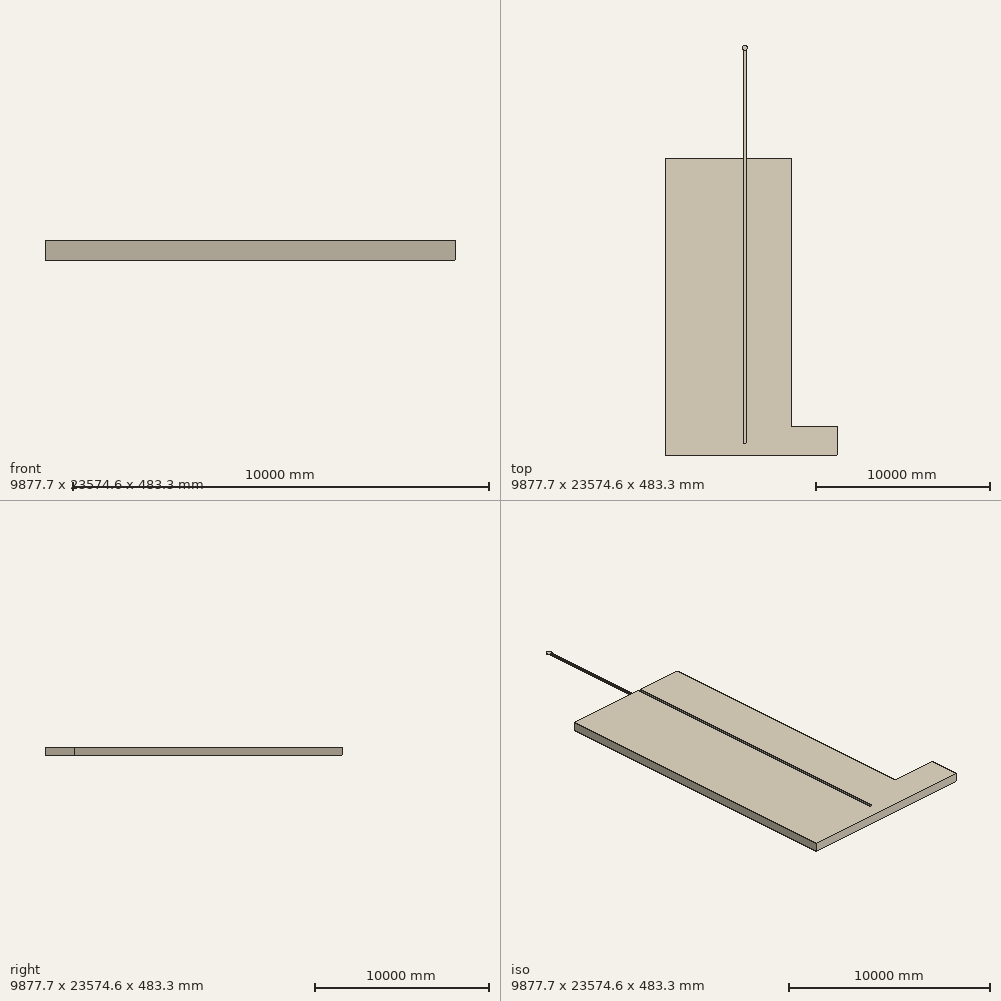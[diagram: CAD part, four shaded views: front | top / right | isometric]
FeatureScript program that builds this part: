
annotation { "Feature Type Name" : "Feature", "Feature Type Description" : "" }
export const myFeature = defineFeature(function(context is Context, id is Id, definition is map)
    precondition{}
    {
        {
            var Q0;
            Q0=qCreatedBy(makeId("Front.planeOp"),FACE);
            var sketch = newSketch(context, id + "F0", { "sketchPlane" : qUnion([Q0])});
            skLineSegment(sketch, "E0.bottom", {"start": v(-11.78, 29.24) * mm, "end": v(-162.05, 29.24) * mm});
            skLineSegment(sketch, "E0.top", {"start": v(-11.78, 3.84) * mm, "end": v(-162.05, 3.84) * mm});
            skLineSegment(sketch, "E0.left", {"start": v(-162.05, 29.24) * mm, "end": v(-162.05, 3.84) * mm});
            skLineSegment(sketch, "E0.right", {"start": v(-11.78, 29.24) * mm, "end": v(-11.78, 3.84) * mm});
            skSolve(sketch);
        }
        {
            var Q0;
            Q0=makeQuery(id+"F0.imprint","IMPRINT",FACE,{"disambiguationData":[TD([[makeQuery(id+"F0.imprint","IMPRINT",EDGE,{"derivedFrom":sQuery(id+"F0.wireOp",EDGE,"E0.bottom")}),1.0]])]});
            extrude(context, id + "F1", {"entities" : qUnion([Q0]), "depth" : 22860 * mm});
        }
        {
            var Q0;
            Q0=makeQuery(id+"F1.opExtrude","SWEPT_FACE",FACE,{"disambiguationData":[OSD([sQuery(id+"F0.wireOp",EDGE,"E0.bottom")])]});
            shell(context, id + "F2", {"entities" : qUnion([Q0]), "thickness" : 1.59 * mm});
        }
        {
            var Q0;
            Q0=makeQuery(id+"F2.opShell","OFFSET_FACE",FACE,{"disambiguationData":[OSD([sQuery(id+"F0.wireOp",EDGE,"E0.top")])]});
            var sketch = newSketch(context, id + "F3", { "sketchPlane" : qUnion([Q0])});
            skCircle(sketch, "E1", {"center": v(-71.32, -114.14) * mm, "radius": 143.58 * mm});
            skSolve(sketch);
        }
        {
            var Q0;
            {var subQ1=sQuery(id+"F0.wireOp",EDGE,"E0.top");var subQ2=makeQuery(id+"F2.opShell","OFFSET_EDGE",EDGE,{"disambiguationData":[OSD([subQ1]),TDD([makeQuery(id+"F1.opExtrude","CAP_EDGE",EDGE,{"disambiguationData":[OSD([subQ1])],"isStart":true})])]});Q0=makeQuery(id+"F3.imprint","IMPRINT",FACE,{"disambiguationData":[TD([[makeQuery(id+"F3.imprint","IMPRINT",EDGE,{"derivedFrom":subQ2}),-1.0]])]});}
            var Q1;
            {var subQ1=sQuery(id+"F0.wireOp",EDGE,"E0.top");var subQ6=makeQuery(id+"F2.opShell","OFFSET_EDGE",EDGE,{"disambiguationData":[OSD([subQ1]),TDD([makeQuery(id+"F1.opExtrude","CAP_EDGE",EDGE,{"disambiguationData":[OSD([subQ1])],"isStart":true})])]});Q1=makeQuery(id+"F3.imprint","IMPRINT",FACE,{"disambiguationData":[TD([[makeQuery(id+"F3.imprint","IMPRINT",EDGE,{"derivedFrom":subQ6}),1.0]])]});}
            var Q2;
            {var subQ0=sQuery(id+"F3.wireOp",EDGE,"E1");var subQ1=sQuery(id+"F0.wireOp",EDGE,"E0.top");var subQ2=makeQuery(id+"F2.opShell","OFFSET_EDGE",EDGE,{"disambiguationData":[OSD([subQ1,sQuery(id+"F0.wireOp",EDGE,"E0.left")])]});var subQ4=makeQuery(id+"F3.imprint","INTERSECT",VERTEX,{"derivedFrom":[subQ2,subQ0]});Q2=makeQuery(id+"F3.imprint","IMPRINT",FACE,{"disambiguationData":[TD([[makeQuery(id+"F3.imprint","IMPRINT",EDGE,{"disambiguationData":[TD([[subQ4,1.0]])],"derivedFrom":subQ0}),1.0]])]});}
            var Q3;
            {var subQ1=sQuery(id+"F0.wireOp",EDGE,"E0.top");var subQ2=makeQuery(id+"F2.opShell","OFFSET_EDGE",EDGE,{"disambiguationData":[OSD([subQ1]),TDD([makeQuery(id+"F1.opExtrude","CAP_EDGE",EDGE,{"disambiguationData":[OSD([subQ1])],"isStart":true})])]});Q3=makeQuery(id+"F3.imprint","IMPRINT",FACE,{"disambiguationData":[TD([[makeQuery(id+"F3.imprint","IMPRINT",EDGE,{"derivedFrom":subQ2}),-1.0]])]});}
            var Q4;
            {var subQ1=sQuery(id+"F0.wireOp",EDGE,"E0.top");var subQ6=makeQuery(id+"F2.opShell","OFFSET_EDGE",EDGE,{"disambiguationData":[OSD([subQ1]),TDD([makeQuery(id+"F1.opExtrude","CAP_EDGE",EDGE,{"disambiguationData":[OSD([subQ1])],"isStart":true})])]});Q4=makeQuery(id+"F3.imprint","IMPRINT",FACE,{"disambiguationData":[TD([[makeQuery(id+"F3.imprint","IMPRINT",EDGE,{"derivedFrom":subQ6}),1.0]])]});}
            extrude(context, id + "F4", {"entities" : qUnion([Q0, Q1, Q2, Q3, Q4]), "operationType" : NewBodyOperationType.ADD, "depth" : 25.4 * mm});
        }
        {
            var Q0;
            Q0=makeQuery(id+"F2.opShell","OFFSET_FACE",FACE,{"disambiguationData":[OSD([sQuery(id+"F0.wireOp",EDGE,"E0.top")])]});
            var sketch = newSketch(context, id + "F5", { "sketchPlane" : qUnion([Q0])});
            skLineSegment(sketch, "E2.bottom", {"start": v(2602.83, -6484.61) * mm, "end": v(-4650.3, -6484.61) * mm});
            skLineSegment(sketch, "E2.top", {"start": v(2602.83, -21867.56) * mm, "end": v(-4650.3, -21867.56) * mm});
            skLineSegment(sketch, "E2.left", {"start": v(2602.83, -6484.61) * mm, "end": v(2602.83, -21867.56) * mm});
            skLineSegment(sketch, "E2.right", {"start": v(-4650.3, -6484.61) * mm, "end": v(-4650.3, -21867.56) * mm});
            skLineSegment(sketch, "E3.bottom", {"start": v(-4650.3, -21867.56) * mm, "end": v(5227.4, -21867.56) * mm});
            skLineSegment(sketch, "E3.top", {"start": v(-4650.3, -23545.2) * mm, "end": v(5227.4, -23545.2) * mm});
            skLineSegment(sketch, "E3.left", {"start": v(-4650.3, -21867.56) * mm, "end": v(-4650.3, -23545.2) * mm});
            skLineSegment(sketch, "E3.right", {"start": v(5227.4, -21867.56) * mm, "end": v(5227.4, -23545.2) * mm});
            skSolve(sketch);
        }
        {
            var Q0;
            {var subQ0=sQuery(id+"F5.wireOp",EDGE,"E2.right");Q0=makeQuery(id+"F5.imprint","IMPRINT",FACE,{"disambiguationData":[TD([[makeQuery(id+"F5.imprint","IMPRINT",EDGE,{"derivedFrom":subQ0}),1.0]])]});}
            var Q1;
            Q1=makeQuery(id+"F5.imprint","IMPRINT",FACE,{"disambiguationData":[TD([[makeQuery(id+"F5.imprint","IMPRINT",EDGE,{"derivedFrom":sQuery(id+"F5.wireOp",EDGE,"E3.top")}),1.0]])]});
            var Q2;
            {var subQ0=sQuery(id+"F5.wireOp",EDGE,"E2.left");Q2=makeQuery(id+"F5.imprint","IMPRINT",FACE,{"disambiguationData":[TD([[makeQuery(id+"F5.imprint","IMPRINT",EDGE,{"derivedFrom":subQ0}),-1.0]])]});}
            extrude(context, id + "F6", {"entities" : qUnion([Q0, Q1, Q2]), "operationType" : NewBodyOperationType.ADD, "depth" : 481.75 * mm});
        }
    });
